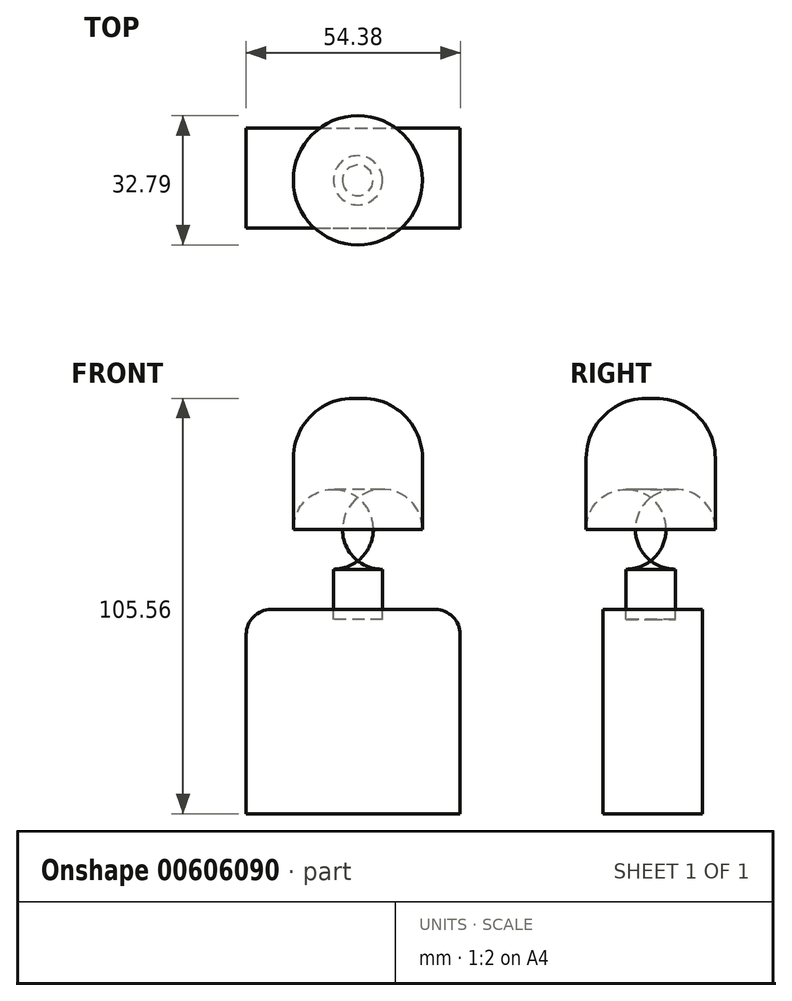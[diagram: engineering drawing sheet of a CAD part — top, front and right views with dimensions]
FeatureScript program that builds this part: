
annotation { "Feature Type Name" : "Feature", "Feature Type Description" : "" }
export const myFeature = defineFeature(function(context is Context, id is Id, definition is map)
    precondition{}
    {
        {
            var Q0;
            Q0=qCreatedBy(makeId("Top.planeOp"),FACE);
            var sketch = newSketch(context, id + "F0", { "sketchPlane" : qUnion([Q0])});
            skCircle(sketch, "E0", {"center": v(-29.49, 18.54) * mm, "radius": 16.4 * mm});
            skSolve(sketch);
        }
        {
            var Q0;
            Q0 = qSketchRegion(id + "F0", true);
            extrude(context, id + "F1", {"entities" : qUnion([Q0]), "depth" : 43.43 * mm, "offsetDistance" : 25.4 * mm});
        }
        {
            var Q0;
            Q0=makeQuery(id+"F1.opExtrude","CAP_FACE",FACE,{"disambiguationData":[OSD([sQuery(id+"F0.wireOp",EDGE,"E0")])],"isStart":false});
            fillet(context, id + "F2", {"entities" : qUnion([Q0]), "radius" : 15.24 * mm, "tangentPropagation" : true, "allowEdgeOverflow" : false});
        }
        {
            var Q0;
            Q0=makeQuery(id+"F1.opExtrude","CAP_FACE",FACE,{"disambiguationData":[OSD([sQuery(id+"F0.wireOp",EDGE,"E0")])],"isStart":true});
            fillet(context, id + "F3", {"entities" : qUnion([Q0]), "radius" : 10.16 * mm, "tangentPropagation" : true, "allowEdgeOverflow" : false});
        }
        {
            var Q0;
            Q0=makeQuery(id+"F1.opExtrude","CAP_FACE",FACE,{"disambiguationData":[OSD([sQuery(id+"F0.wireOp",EDGE,"E0")])],"isStart":true});
            extrude(context, id + "F4", {"entities" : qUnion([Q0]), "operationType" : NewBodyOperationType.ADD, "depth" : 12.7 * mm, "offsetDistance" : 25.4 * mm});
        }
        {
            var Q0;
            Q0=qCreatedBy(makeId("Front.planeOp"),FACE);
            var sketch = newSketch(context, id + "F5", { "sketchPlane" : qUnion([Q0])});
            skLineSegment(sketch, "E1.bottom", {"start": v(-49.73, -10.22) * mm, "end": v(-8.05, -10.22) * mm});
            skLineSegment(sketch, "E1.top", {"start": v(-56.08, -62.13) * mm, "end": v(-1.7, -62.13) * mm});
            skLineSegment(sketch, "E1.left", {"start": v(-56.08, -16.57) * mm, "end": v(-56.08, -62.13) * mm});
            skLineSegment(sketch, "E1.right", {"start": v(-1.7, -16.57) * mm, "end": v(-1.7, -62.13) * mm});
            skPoint(sketch, "E2.visualSharp", {"position": v(-56.08, -10.22) * mm});
            skArc(sketch, "E2.filletArc", {"start": v(-49.73, -10.22) * mm, "mid": v(-54.22, -12.08) * mm, "end": v(-56.08, -16.57) * mm});
            skPoint(sketch, "E3.visualSharp", {"position": v(-1.7, -10.22) * mm});
            skArc(sketch, "E3.filletArc", {"start": v(-1.7, -16.57) * mm, "mid": v(-3.56, -12.08) * mm, "end": v(-8.05, -10.22) * mm});
            skSolve(sketch);
        }
        {
            var Q0;
            Q0 = qSketchRegion(id + "F5", true);
            extrude(context, id + "F6", {"entities" : qUnion([Q0]), "depth" : 25.4 * mm, "offsetDistance" : 25.4 * mm});
        }
        {
            var Q0;
            Q0=makeQuery(id+"F6.opExtrude","SWEPT_BODY",BODY,{"disambiguationData":[OSD([sQuery(id+"F5.wireOp",EDGE,"E1.bottom"),sQuery(id+"F5.wireOp",EDGE,"E1.top"),sQuery(id+"F5.wireOp",EDGE,"E1.left"),sQuery(id+"F5.wireOp",EDGE,"E1.right"),sQuery(id+"F5.wireOp",EDGE,"E2.filletArc"),sQuery(id+"F5.wireOp",EDGE,"E3.filletArc")])]});
            transform(context, id + "F7", {"entities" : qUnion([Q0]), "transformType" : TransformType.TRANSLATION_3D, "dx" : -1.78 * mm, "dy" : 31.75 * mm, "dz" : 0 * mm, "makeCopy" : false});
        }
    });
